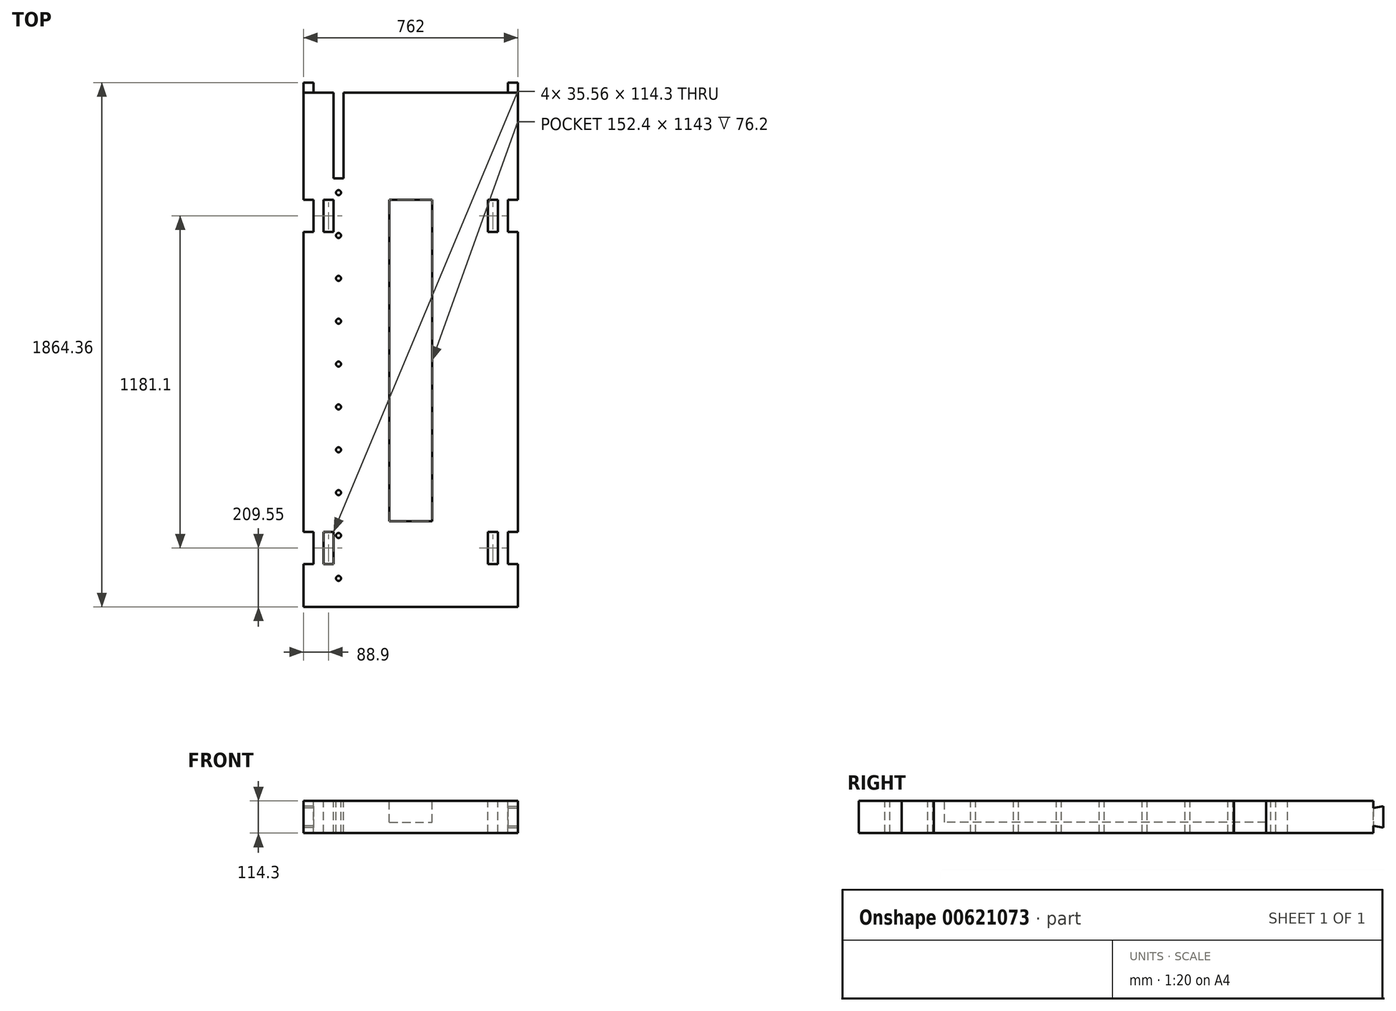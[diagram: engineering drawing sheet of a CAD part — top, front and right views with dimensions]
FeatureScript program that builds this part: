
annotation { "Feature Type Name" : "Feature", "Feature Type Description" : "" }
export const myFeature = defineFeature(function(context is Context, id is Id, definition is map)
    precondition{}
    {
        {
            var Q0;
            Q0=qCreatedBy(makeId("Top.planeOp"),FACE);
            var sketch = newSketch(context, id + "F0", { "sketchPlane" : qUnion([Q0])});
            skLineSegment(sketch, "E0.bottom", {"start": v(-381, 914.4) * mm, "end": v(381, 914.4) * mm});
            skLineSegment(sketch, "E0.top", {"start": v(-381, -914.4) * mm, "end": v(381, -914.4) * mm});
            skLineSegment(sketch, "E0.left", {"start": v(-381, 914.4) * mm, "end": v(-381, -914.4) * mm});
            skLineSegment(sketch, "E0.right", {"start": v(381, 914.4) * mm, "end": v(381, -914.4) * mm});
            skSolve(sketch);
        }
        {
            var Q0;
            Q0=makeQuery(id+"F0.imprint","IMPRINT",FACE,{"disambiguationData":[TD([[makeQuery(id+"F0.imprint","IMPRINT",EDGE,{"derivedFrom":sQuery(id+"F0.wireOp",EDGE,"E0.bottom")}),-1.0]])]});
            extrude(context, id + "F1", {"entities" : qUnion([Q0]), "depth" : 114.3 * mm, "offsetDistance" : 25.4 * mm});
        }
        {
            var Q0;
            Q0=makeQuery(id+"F1.opExtrude","CAP_FACE",FACE,{"disambiguationData":[OSD([sQuery(id+"F0.wireOp",EDGE,"E0.bottom"),sQuery(id+"F0.wireOp",EDGE,"E0.top"),sQuery(id+"F0.wireOp",EDGE,"E0.left"),sQuery(id+"F0.wireOp",EDGE,"E0.right")])],"isStart":false});
            var sketch = newSketch(context, id + "F2", { "sketchPlane" : qUnion([Q0])});
            skLineSegment(sketch, "E1.bottom", {"start": v(-309.88, 533.4) * mm, "end": v(-274.32, 533.4) * mm});
            skLineSegment(sketch, "E1.top", {"start": v(-309.88, 419.1) * mm, "end": v(-274.32, 419.1) * mm});
            skLineSegment(sketch, "E1.left", {"start": v(-309.88, 533.4) * mm, "end": v(-309.88, 419.1) * mm});
            skLineSegment(sketch, "E1.right", {"start": v(-274.32, 533.4) * mm, "end": v(-274.32, 419.1) * mm});
            skLineSegment(sketch, "E2.bottom", {"start": v(274.32, 533.4) * mm, "end": v(309.88, 533.4) * mm});
            skLineSegment(sketch, "E2.top", {"start": v(274.32, 419.1) * mm, "end": v(309.88, 419.1) * mm});
            skLineSegment(sketch, "E2.left", {"start": v(274.32, 533.4) * mm, "end": v(274.32, 419.1) * mm});
            skLineSegment(sketch, "E2.right", {"start": v(309.88, 533.4) * mm, "end": v(309.88, 419.1) * mm});
            skLineSegment(sketch, "E3.bottom", {"start": v(-309.88, -647.7) * mm, "end": v(-274.32, -647.7) * mm});
            skLineSegment(sketch, "E3.top", {"start": v(-309.88, -762) * mm, "end": v(-274.32, -762) * mm});
            skLineSegment(sketch, "E3.left", {"start": v(-309.88, -647.7) * mm, "end": v(-309.88, -762) * mm});
            skLineSegment(sketch, "E3.right", {"start": v(-274.32, -647.7) * mm, "end": v(-274.32, -762) * mm});
            skLineSegment(sketch, "E4.bottom", {"start": v(274.32, -647.7) * mm, "end": v(309.88, -647.7) * mm});
            skLineSegment(sketch, "E4.top", {"start": v(274.32, -762) * mm, "end": v(309.88, -762) * mm});
            skLineSegment(sketch, "E4.left", {"start": v(274.32, -647.7) * mm, "end": v(274.32, -762) * mm});
            skLineSegment(sketch, "E4.right", {"start": v(309.88, -647.7) * mm, "end": v(309.88, -762) * mm});
            skLineSegment(sketch, "E5", {"start": v(-345.44, 533.4) * mm, "end": v(-381, 533.4) * mm});
            skLineSegment(sketch, "E6", {"start": v(-381, 533.4) * mm, "end": v(-381, 419.1) * mm});
            skLineSegment(sketch, "E7", {"start": v(-381, 419.1) * mm, "end": v(-345.44, 419.1) * mm});
            skLineSegment(sketch, "E8", {"start": v(-345.44, 419.1) * mm, "end": v(-345.44, 533.4) * mm});
            skLineSegment(sketch, "E9", {"start": v(-381, -647.7) * mm, "end": v(-345.44, -647.7) * mm});
            skLineSegment(sketch, "E10", {"start": v(-345.44, -647.7) * mm, "end": v(-345.44, -762) * mm});
            skLineSegment(sketch, "E11", {"start": v(-345.44, -762) * mm, "end": v(-381, -762) * mm});
            skLineSegment(sketch, "E12", {"start": v(-381, -762) * mm, "end": v(-381, -647.7) * mm});
            skLineSegment(sketch, "E13", {"start": v(345.44, 533.4) * mm, "end": v(345.44, 419.1) * mm});
            skLineSegment(sketch, "E14", {"start": v(345.44, 419.1) * mm, "end": v(381, 419.1) * mm});
            skLineSegment(sketch, "E15", {"start": v(381, 419.1) * mm, "end": v(381, 533.4) * mm});
            skLineSegment(sketch, "E16", {"start": v(381, 533.4) * mm, "end": v(345.44, 533.4) * mm});
            skLineSegment(sketch, "E17", {"start": v(345.44, -762) * mm, "end": v(345.44, -647.7) * mm});
            skLineSegment(sketch, "E18", {"start": v(345.44, -647.7) * mm, "end": v(381, -647.7) * mm});
            skLineSegment(sketch, "E19", {"start": v(381, -647.7) * mm, "end": v(381, -762) * mm});
            skLineSegment(sketch, "E20", {"start": v(381, -762) * mm, "end": v(345.44, -762) * mm});
            skSolve(sketch);
        }
        {
            var Q0;
            Q0 = qSketchRegion(id + "F2", true);
            var Q1;
            Q1=makeQuery(id+"F1.opExtrude","CAP_FACE",FACE,{"disambiguationData":[OSD([sQuery(id+"F0.wireOp",EDGE,"E0.bottom"),sQuery(id+"F0.wireOp",EDGE,"E0.top"),sQuery(id+"F0.wireOp",EDGE,"E0.left"),sQuery(id+"F0.wireOp",EDGE,"E0.right")])],"isStart":true});
            extrude(context, id + "F3", {"entities" : qUnion([Q0]), "operationType" : NewBodyOperationType.REMOVE, "endBound" : BoundingType.UP_TO_SURFACE, "oppositeDirection" : true, "depth" : 25.4 * mm, "endBoundEntityFace" : qUnion([Q1]), "offsetDistance" : 25.4 * mm});
        }
        {
            var Q0;
            Q0=makeQuery(id+"F1.opExtrude","CAP_FACE",FACE,{"disambiguationData":[OSD([sQuery(id+"F0.wireOp",EDGE,"E0.bottom"),sQuery(id+"F0.wireOp",EDGE,"E0.top"),sQuery(id+"F0.wireOp",EDGE,"E0.left"),sQuery(id+"F0.wireOp",EDGE,"E0.right")])],"isStart":false});
            var sketch = newSketch(context, id + "F4", { "sketchPlane" : qUnion([Q0])});
            skLineSegment(sketch, "E21.bottom", {"start": v(-76.2, 533.4) * mm, "end": v(76.2, 533.4) * mm});
            skLineSegment(sketch, "E21.top", {"start": v(-76.2, -609.6) * mm, "end": v(76.2, -609.6) * mm});
            skLineSegment(sketch, "E21.left", {"start": v(-76.2, 533.4) * mm, "end": v(-76.2, -609.6) * mm});
            skLineSegment(sketch, "E21.right", {"start": v(76.2, 533.4) * mm, "end": v(76.2, -609.6) * mm});
            skSolve(sketch);
        }
        {
            var Q0;
            Q0 = qSketchRegion(id + "F4", true);
            extrude(context, id + "F5", {"entities" : qUnion([Q0]), "operationType" : NewBodyOperationType.REMOVE, "oppositeDirection" : true, "depth" : 76.2 * mm, "offsetDistance" : 25.4 * mm});
        }
        {
            var Q0;
            Q0=makeQuery(id+"F1.opExtrude","CAP_FACE",FACE,{"disambiguationData":[OSD([sQuery(id+"F0.wireOp",EDGE,"E0.bottom"),sQuery(id+"F0.wireOp",EDGE,"E0.top"),sQuery(id+"F0.wireOp",EDGE,"E0.left"),sQuery(id+"F0.wireOp",EDGE,"E0.right")])],"isStart":false});
            var sketch = newSketch(context, id + "F6", { "sketchPlane" : qUnion([Q0])});
            skLineSegment(sketch, "E22.bottom", {"start": v(-274.32, 914.4) * mm, "end": v(-238.76, 914.4) * mm});
            skLineSegment(sketch, "E22.top", {"start": v(-274.32, 609.6) * mm, "end": v(-238.76, 609.6) * mm});
            skLineSegment(sketch, "E22.left", {"start": v(-274.32, 914.4) * mm, "end": v(-274.32, 609.6) * mm});
            skLineSegment(sketch, "E22.right", {"start": v(-238.76, 914.4) * mm, "end": v(-238.76, 609.6) * mm});
            skSolve(sketch);
        }
        {
            var Q0;
            Q0 = qSketchRegion(id + "F6", true);
            extrude(context, id + "F7", {"entities" : qUnion([Q0]), "operationType" : NewBodyOperationType.REMOVE, "endBound" : BoundingType.UP_TO_NEXT, "oppositeDirection" : true, "depth" : 25.4 * mm, "offsetDistance" : 25.4 * mm});
        }
        {
            var Q0;
            {var subQ0=sQuery(id+"F0.wireOp",EDGE,"E0.bottom");var subQ2=sQuery(id+"F0.wireOp",EDGE,"E0.left");Q0=makeQuery(id+"F3.boolean.opBoolean","SPLIT",FACE,{"disambiguationData":[TD([makeQuery(id+"F1.opExtrude","SWEPT_FACE",FACE,{"disambiguationData":[OSD([subQ0])]})])],"derivedFrom":makeQuery(id+"F1.opExtrude","SWEPT_FACE",FACE,{"disambiguationData":[OSD([subQ2])]})});}
            var sketch = newSketch(context, id + "F8", { "sketchPlane" : qUnion([Q0])});
            skLineSegment(sketch, "E23", {"start": v(-914.4, 88.9) * mm, "end": v(-949.96, 95.17) * mm});
            skLineSegment(sketch, "E24", {"start": v(-949.96, 95.17) * mm, "end": v(-949.96, 19.13) * mm});
            skLineSegment(sketch, "E25", {"start": v(-949.96, 19.13) * mm, "end": v(-914.4, 25.4) * mm});
            skLineSegment(sketch, "E26", {"start": v(-914.4, 25.4) * mm, "end": v(-914.4, 88.9) * mm});
            skSolve(sketch);
        }
        {
            var Q0;
            Q0=makeQuery(id+"F8.imprint","IMPRINT",FACE,{"disambiguationData":[TD([[makeQuery(id+"F8.imprint","IMPRINT",EDGE,{"derivedFrom":sQuery(id+"F8.wireOp",EDGE,"E23")}),1.0]])]});
            extrude(context, id + "F9", {"entities" : qUnion([Q0]), "operationType" : NewBodyOperationType.ADD, "oppositeDirection" : true, "depth" : 35.56 * mm, "offsetDistance" : 25.4 * mm});
        }
        {
            var Q0;
            {var subQ0=sQuery(id+"F0.wireOp",EDGE,"E0.bottom");var subQ1=sQuery(id+"F0.wireOp",EDGE,"E0.right");Q0=makeQuery(id+"F3.boolean.opBoolean","SPLIT",FACE,{"disambiguationData":[TD([makeQuery(id+"F1.opExtrude","SWEPT_FACE",FACE,{"disambiguationData":[OSD([subQ0])]})])],"derivedFrom":makeQuery(id+"F1.opExtrude","SWEPT_FACE",FACE,{"disambiguationData":[OSD([subQ1])]})});}
            var sketch = newSketch(context, id + "F10", { "sketchPlane" : qUnion([Q0])});
            skLineSegment(sketch, "E27", {"start": v(914.4, 88.9) * mm, "end": v(949.96, 95.17) * mm});
            skLineSegment(sketch, "E28", {"start": v(949.96, 95.17) * mm, "end": v(949.96, 19.13) * mm});
            skLineSegment(sketch, "E29", {"start": v(949.96, 19.13) * mm, "end": v(914.4, 25.4) * mm});
            skLineSegment(sketch, "E30", {"start": v(914.4, 25.4) * mm, "end": v(914.4, 88.9) * mm});
            skSolve(sketch);
        }
        {
            var Q0;
            Q0 = qSketchRegion(id + "F10", true);
            extrude(context, id + "F11", {"entities" : qUnion([Q0]), "operationType" : NewBodyOperationType.ADD, "oppositeDirection" : true, "depth" : 35.56 * mm, "offsetDistance" : 25.4 * mm});
        }
        {
            var Q0;
            Q0=makeQuery(id+"F1.opExtrude","CAP_FACE",FACE,{"disambiguationData":[OSD([sQuery(id+"F0.wireOp",EDGE,"E0.bottom"),sQuery(id+"F0.wireOp",EDGE,"E0.top"),sQuery(id+"F0.wireOp",EDGE,"E0.left"),sQuery(id+"F0.wireOp",EDGE,"E0.right")])],"isStart":false});
            var sketch = newSketch(context, id + "F12", { "sketchPlane" : qUnion([Q0])});
            skCircle(sketch, "E31", {"center": v(-256.54, 558.8) * mm, "radius": 8.73 * mm});
            skCircle(sketch, "E32.0.1.0", {"center": v(-256.54, 406.4) * mm, "radius": 8.73 * mm});
            skCircle(sketch, "E32.0.2.0", {"center": v(-256.54, 254) * mm, "radius": 8.73 * mm});
            skCircle(sketch, "E32.0.3.0", {"center": v(-256.54, 101.6) * mm, "radius": 8.73 * mm});
            skCircle(sketch, "E32.0.4.0", {"center": v(-256.54, -50.8) * mm, "radius": 8.73 * mm});
            skCircle(sketch, "E32.0.5.0", {"center": v(-256.54, -203.2) * mm, "radius": 8.73 * mm});
            skCircle(sketch, "E32.0.6.0", {"center": v(-256.54, -355.6) * mm, "radius": 8.73 * mm});
            skCircle(sketch, "E32.0.7.0", {"center": v(-256.54, -508) * mm, "radius": 8.73 * mm});
            skCircle(sketch, "E32.0.8.0", {"center": v(-256.54, -660.4) * mm, "radius": 8.73 * mm});
            skCircle(sketch, "E32.0.9.0", {"center": v(-256.54, -812.8) * mm, "radius": 8.73 * mm});
            skLineSegment(sketch, "E32.direction1", {"start": v(-256.54, 558.8) * mm, "end": v(-231.14, 558.8) * mm, "construction": true});
            skLineSegment(sketch, "E32.direction2", {"start": v(-256.54, 558.8) * mm, "end": v(-256.54, 406.4) * mm, "construction": true});
            skSolve(sketch);
        }
        {
            var Q0;
            Q0 = qSketchRegion(id + "F12", true);
            extrude(context, id + "F13", {"entities" : qUnion([Q0]), "operationType" : NewBodyOperationType.REMOVE, "endBound" : BoundingType.UP_TO_NEXT, "oppositeDirection" : true, "depth" : 25.4 * mm, "offsetDistance" : 25.4 * mm});
        }
    });
